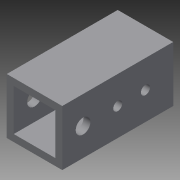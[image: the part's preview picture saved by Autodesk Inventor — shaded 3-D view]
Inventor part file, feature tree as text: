
AUTODESK INVENTOR PART (.ipt)
format: ipt  version: 2014 (Build 180170000, 170)  size: 100,864 bytes
history: native  units: in
note: dims shown in document units (in); Inventor stores cm internally (conversion verified against a paired STEP export)
features: extrude x2, sketch x2
ambient origin geometry x8: Origin, YZ Plane, XZ Plane, XY Plane, X Axis, Y Axis, Z Axis, Center Point
bodies: Solid1 (feature_tree)
feature tree (4):
  extrude  "Extrusion1"  Depth=1.0in
  extrude  "Extrusion2"  Depth=2.0in TaperAngle=0.0deg
  sketch  "Sketch1"  dims[d0=1.0in d1=1.0in]
  sketch  "Sketch2"  dims[d2=0.125in d3=2.0in d4=0.0in d5=0.266in d6=0.5in d7=0.375in d8=0.163in d9=0.5in d10=0.5in d11=0.7874in d13=0.5in d14=0.3937in d16=1.0in d18=2.0in d19=0.0in]
